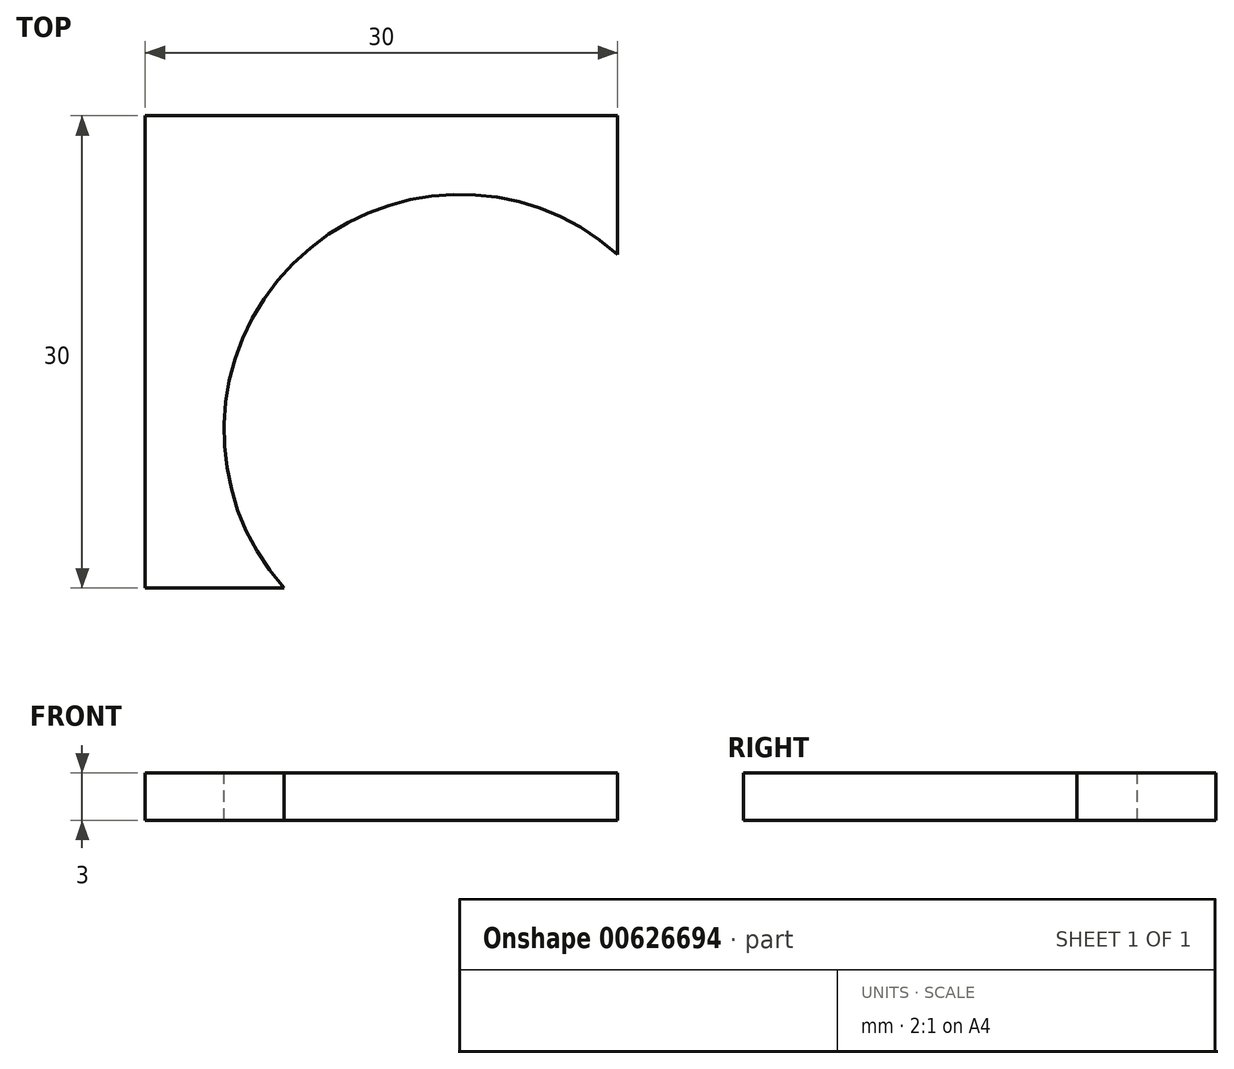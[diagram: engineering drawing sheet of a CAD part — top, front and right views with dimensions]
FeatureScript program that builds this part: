
annotation { "Feature Type Name" : "Feature", "Feature Type Description" : "" }
export const myFeature = defineFeature(function(context is Context, id is Id, definition is map)
    precondition{}
    {
        {
            var Q0;
            Q0=qCreatedBy(makeId("Top.planeOp"),FACE);
            var sketch = newSketch(context, id + "F0", { "sketchPlane" : qUnion([Q0])});
            skCircle(sketch, "E0", {"center": v(0, 0) * mm, "radius": 15 * mm});
            skCircle(sketch, "E1", {"center": v(0, 10) * mm, "radius": 2.5 * mm});
            skSolve(sketch);
        }
        {
            var Q0;
            Q0=makeQuery(id+"F0.imprint","IMPRINT",FACE,{"disambiguationData":[TD([[makeQuery(id+"F0.imprint","IMPRINT",EDGE,{"derivedFrom":sQuery(id+"F0.wireOp",EDGE,"E0")}),1.0]])]});
            extrude(context, id + "F1", {"entities" : qUnion([Q0]), "oppositeDirection" : true, "depth" : 3 * mm, "offsetDistance" : 25 * mm});
        }
        {
            var Q0;
            Q0=qCreatedBy(makeId("Top.planeOp"),FACE);
            var sketch = newSketch(context, id + "F2", { "sketchPlane" : qUnion([Q0])});
            skText(sketch, "E2", { "text": "OBR", "fontName": "AllertaStencil-Regular.ttf"});
            skPoint(sketch, "E3", {"position": v(0, 0) * mm});
            const initialGuessF2  = {"E2": [-0.01138, -0.004, 1, 0, 0.008]};
            skSetInitialGuess(sketch, initialGuessF2);
            skSolve(sketch);
        }
        {
            var Q0;
            Q0 = qSketchRegion(id + "F2", true);
            extrude(context, id + "F3", {"entities" : qUnion([Q0]), "operationType" : NewBodyOperationType.REMOVE, "endBound" : BoundingType.THROUGH_ALL, "oppositeDirection" : true, "depth" : 25 * mm, "offsetDistance" : 25 * mm});
        }
        {
            var Q0;
            Q0=qCreatedBy(makeId("Top.planeOp"),FACE);
            var sketch = newSketch(context, id + "F4", { "sketchPlane" : qUnion([Q0])});
            skLineSegment(sketch, "E4.bottom", {"start": v(-7.43, 4.12) * mm, "end": v(-7, 4.12) * mm});
            skLineSegment(sketch, "E4.top", {"start": v(-7.43, -4.05) * mm, "end": v(-7, -4.05) * mm});
            skLineSegment(sketch, "E4.left", {"start": v(-7.43, 4.12) * mm, "end": v(-7.43, -4.05) * mm});
            skLineSegment(sketch, "E4.right", {"start": v(-7, 4.12) * mm, "end": v(-7, -4.05) * mm});
            skLineSegment(sketch, "E5.bottom", {"start": v(-0.7, 4) * mm, "end": v(-0.26, 4) * mm});
            skLineSegment(sketch, "E5.top", {"start": v(-0.7, -4) * mm, "end": v(-0.26, -4) * mm});
            skLineSegment(sketch, "E5.left", {"start": v(-0.7, 4) * mm, "end": v(-0.7, -4) * mm});
            skLineSegment(sketch, "E5.right", {"start": v(-0.26, 4) * mm, "end": v(-0.26, -4) * mm});
            skLineSegment(sketch, "E6.bottom", {"start": v(6.51, 4) * mm, "end": v(6.96, 4) * mm});
            skLineSegment(sketch, "E6.top", {"start": v(6.51, -1.11) * mm, "end": v(6.96, -1.11) * mm});
            skLineSegment(sketch, "E6.left", {"start": v(6.51, 4) * mm, "end": v(6.51, -1.11) * mm});
            skLineSegment(sketch, "E6.right", {"start": v(6.96, 4) * mm, "end": v(6.96, -1.11) * mm});
            skSolve(sketch);
        }
        {
            var Q0;
            Q0 = qSketchRegion(id + "F4", true);
            extrude(context, id + "F5", {"entities" : qUnion([Q0]), "operationType" : NewBodyOperationType.REMOVE, "endBound" : BoundingType.THROUGH_ALL, "oppositeDirection" : true, "depth" : 25 * mm, "offsetDistance" : 25 * mm});
        }
        {
            var Q0;
            Q0=makeQuery(id+"F5.boolean.opBoolean","SPLIT",BODY,{"disambiguationData":[OD(1.0)],"derivedFrom":makeQuery(id+"F1.opExtrude","SWEPT_BODY",BODY,{"disambiguationData":[OSD([sQuery(id+"F0.wireOp",EDGE,"E0")])]})});
            var Q1;
            Q1=makeQuery(id+"F5.boolean.opBoolean","SPLIT",BODY,{"disambiguationData":[OD(2.0)],"derivedFrom":makeQuery(id+"F1.opExtrude","SWEPT_BODY",BODY,{"disambiguationData":[OSD([sQuery(id+"F0.wireOp",EDGE,"E0")])]})});
            var Q2;
            Q2=makeQuery(id+"F5.boolean.opBoolean","SPLIT",BODY,{"disambiguationData":[OD(3.0)],"derivedFrom":makeQuery(id+"F1.opExtrude","SWEPT_BODY",BODY,{"disambiguationData":[OSD([sQuery(id+"F0.wireOp",EDGE,"E0")])]})});
            var Q3;
            Q3=makeQuery(id+"F5.boolean.opBoolean","SPLIT",BODY,{"disambiguationData":[OD(4.0)],"derivedFrom":makeQuery(id+"F1.opExtrude","SWEPT_BODY",BODY,{"disambiguationData":[OSD([sQuery(id+"F0.wireOp",EDGE,"E0")])]})});
            var Q4;
            Q4=makeQuery(id+"F5.boolean.opBoolean","SPLIT",BODY,{"disambiguationData":[OD(5.0)],"derivedFrom":makeQuery(id+"F1.opExtrude","SWEPT_BODY",BODY,{"disambiguationData":[OSD([sQuery(id+"F0.wireOp",EDGE,"E0")])]})});
            deleteBodies(context, id + "F6", {"entities" : qUnion([Q0, Q1, Q2, Q3, Q4])});
        }
        {
            var Q0;
            Q0=qCreatedBy(makeId("Top.planeOp"),FACE);
            var sketch = newSketch(context, id + "F7", { "sketchPlane" : qUnion([Q0])});
            skLineSegment(sketch, "E7.bottom", {"start": v(-20, 20) * mm, "end": v(10, 20) * mm});
            skLineSegment(sketch, "E7.top", {"start": v(-20, -10) * mm, "end": v(-11.18, -10) * mm});
            skLineSegment(sketch, "E7.left", {"start": v(-20, 20) * mm, "end": v(-20, -10) * mm});
            skLineSegment(sketch, "E7.right", {"start": v(10, 20) * mm, "end": v(10, 11.18) * mm});
            skArc(sketch, "E8", {"start": v(-11.18, -10) * mm, "mid": v(-10.6, 10.6) * mm, "end": v(10, 11.18) * mm});
            skSolve(sketch);
        }
        {
            var Q0;
            Q0 = qSketchRegion(id + "F7", true);
            extrude(context, id + "F8", {"entities" : qUnion([Q0]), "oppositeDirection" : true, "depth" : 3 * mm, "offsetDistance" : 25 * mm});
        }
    });
